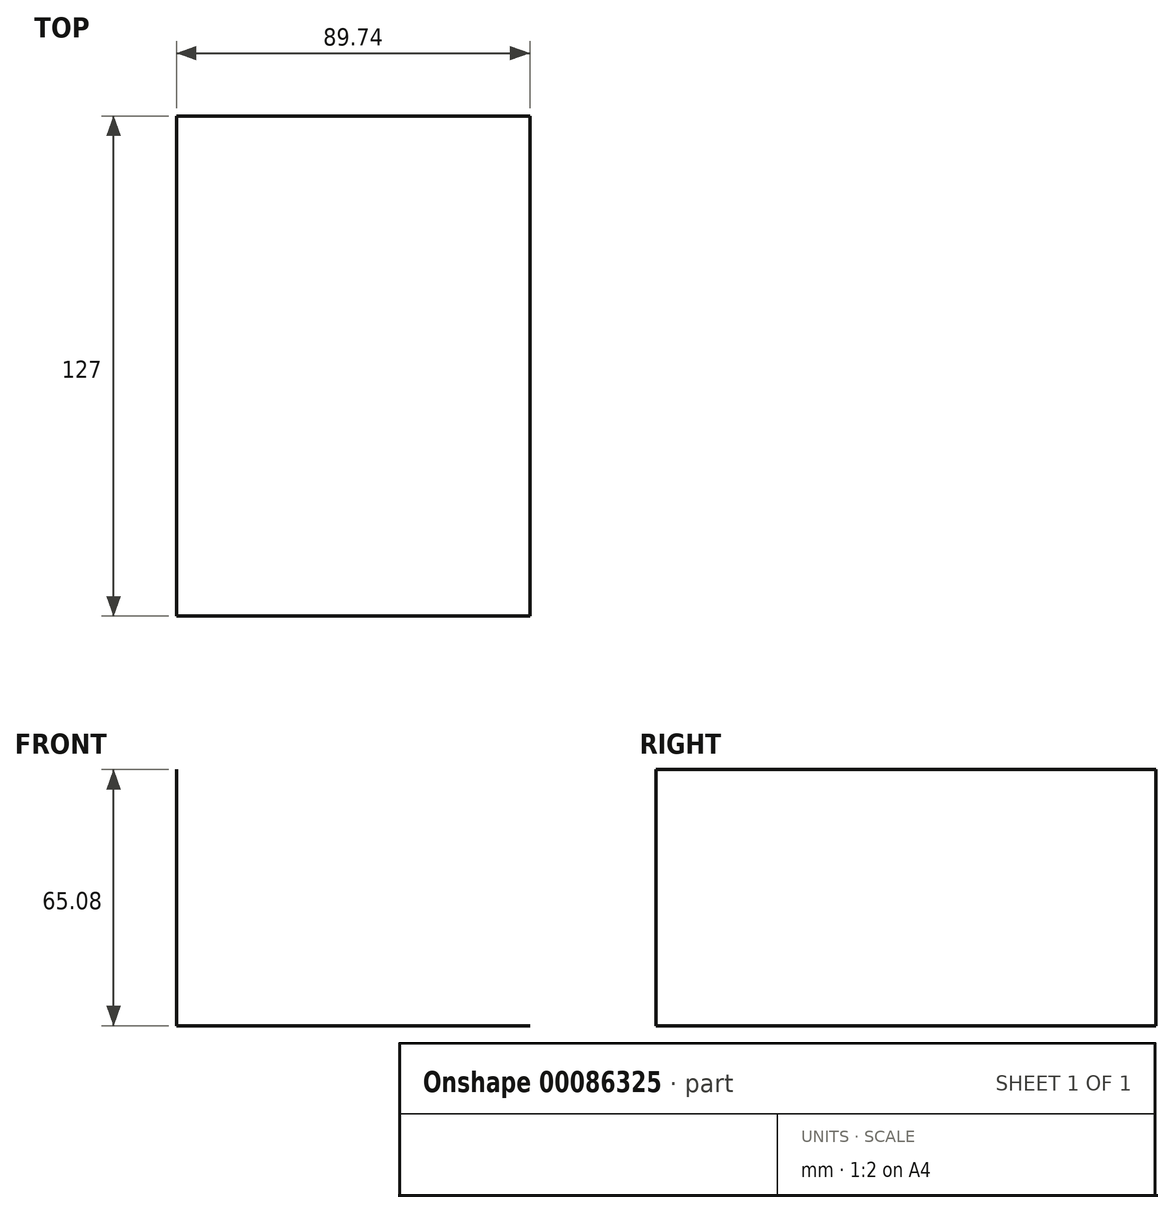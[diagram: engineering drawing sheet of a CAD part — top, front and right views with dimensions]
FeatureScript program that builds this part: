
annotation { "Feature Type Name" : "Feature", "Feature Type Description" : "" }
export const myFeature = defineFeature(function(context is Context, id is Id, definition is map)
    precondition{}
    {
        {
            var Q0;
            Q0=qCreatedBy(makeId("Front.planeOp"),FACE);
            var sketch = newSketch(context, id + "F0", { "sketchPlane" : qUnion([Q0])});
            skLineSegment(sketch, "E0.bottom", {"start": v(-43.76, 40.33) * mm, "end": v(45.98, 40.33) * mm});
            skLineSegment(sketch, "E0.top", {"start": v(-43.76, -24.75) * mm, "end": v(45.98, -24.75) * mm});
            skLineSegment(sketch, "E0.left", {"start": v(-43.76, 40.33) * mm, "end": v(-43.76, -24.75) * mm});
            skLineSegment(sketch, "E0.right", {"start": v(45.98, 40.33) * mm, "end": v(45.98, -24.75) * mm});
            skSolve(sketch);
        }
        {
            var Q0;
            Q0=sQuery(id+"F0.wireOp",EDGE,"E0.top");
            var Q1;
            Q1=sQuery(id+"F0.wireOp",EDGE,"E0.left");
            extrude(context, id + "F1", {"bodyType" : ToolBodyType.SURFACE, "surfaceEntities" : qUnion([Q0, Q1]), "depth" : 127 * mm});
        }
    });
